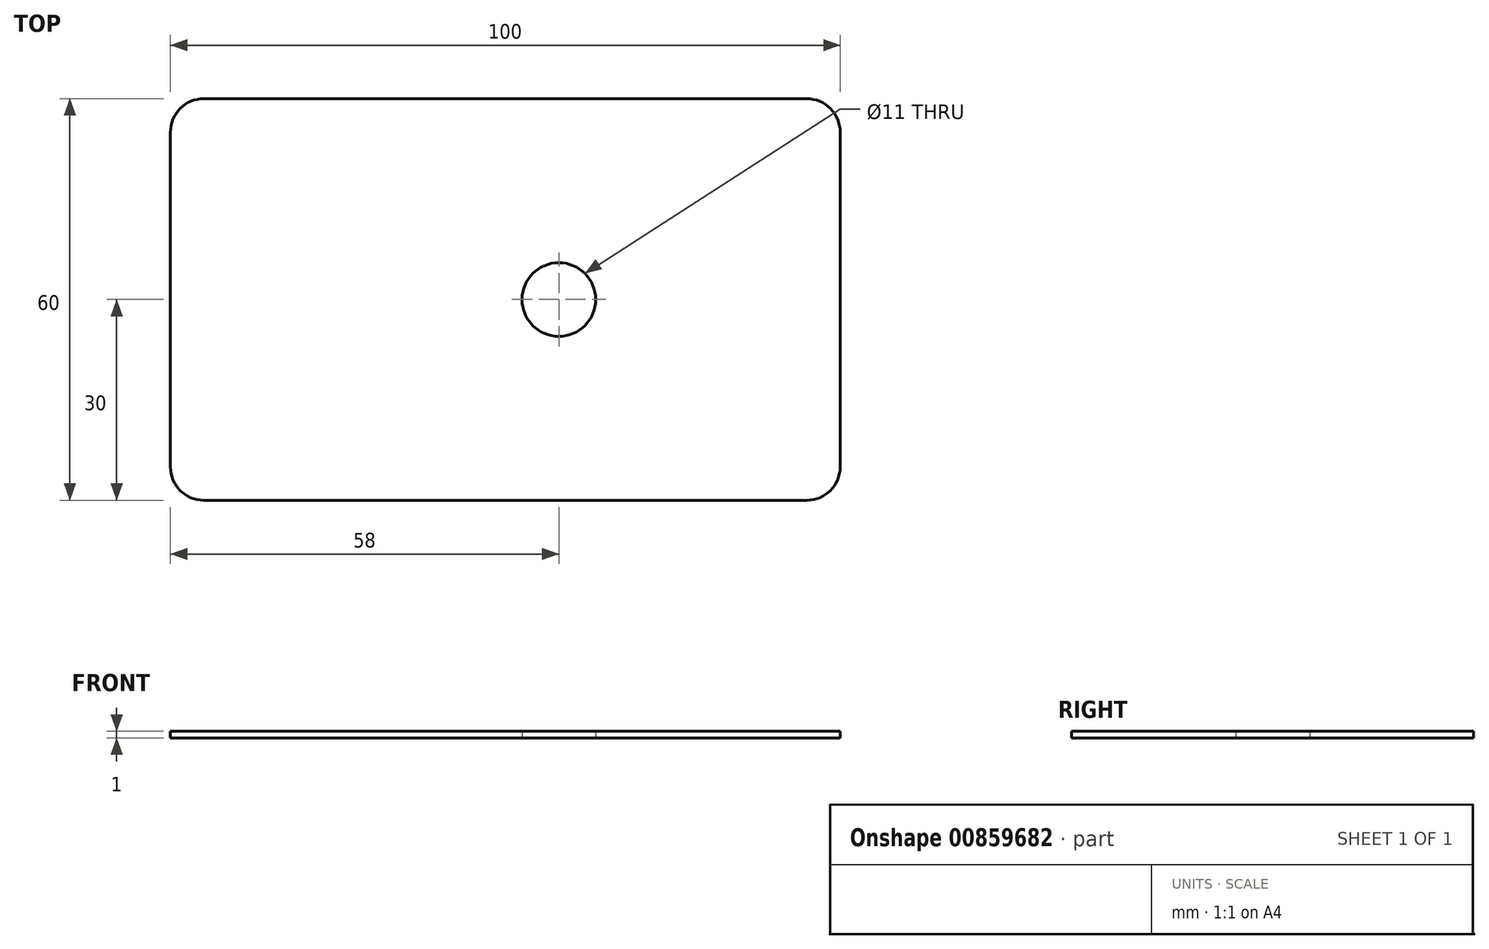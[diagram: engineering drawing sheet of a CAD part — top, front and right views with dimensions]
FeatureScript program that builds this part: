
annotation { "Feature Type Name" : "Feature", "Feature Type Description" : "" }
export const myFeature = defineFeature(function(context is Context, id is Id, definition is map)
    precondition{}
    {
        {
            var Q0;
            Q0=qCreatedBy(makeId("Top.planeOp"),FACE);
            var sketch = newSketch(context, id + "F0", { "sketchPlane" : qUnion([Q0])});
            skLineSegment(sketch, "E0.0.0", {"start": v(42, -25) * mm, "end": v(42, 25) * mm});
            skArc(sketch, "E0.0.1", {"start": v(42, 25) * mm, "mid": v(40.54, 28.54) * mm, "end": v(37, 30) * mm});
            skLineSegment(sketch, "E0.0.2", {"start": v(37, 30) * mm, "end": v(-53, 30) * mm});
            skArc(sketch, "E0.0.3", {"start": v(-53, 30) * mm, "mid": v(-56.54, 28.54) * mm, "end": v(-58, 25) * mm});
            skLineSegment(sketch, "E0.0.4", {"start": v(-58, 25) * mm, "end": v(-58, -25) * mm});
            skArc(sketch, "E0.0.5", {"start": v(-58, -25) * mm, "mid": v(-56.54, -28.54) * mm, "end": v(-53, -30) * mm});
            skLineSegment(sketch, "E0.0.6", {"start": v(-53, -30) * mm, "end": v(37, -30) * mm});
            skArc(sketch, "E0.0.7", {"start": v(37, -30) * mm, "mid": v(40.54, -28.54) * mm, "end": v(42, -25) * mm});
            skCircle(sketch, "E1.0", {"center": v(0, 0) * mm, "radius": 5.5 * mm});
            skSolve(sketch);
        }
        {
            var Q0;
            Q0=makeQuery(id+"F0.imprint","IMPRINT",FACE,{"disambiguationData":[TD([[makeQuery(id+"F0.imprint","IMPRINT",EDGE,{"derivedFrom":sQuery(id+"F0.wireOp",EDGE,"E0.0.0")}),1.0]])]});
            extrude(context, id + "F1", {"entities" : qUnion([Q0]), "depth" : 1 * mm, "offsetDistance" : 25 * mm});
        }
    });
